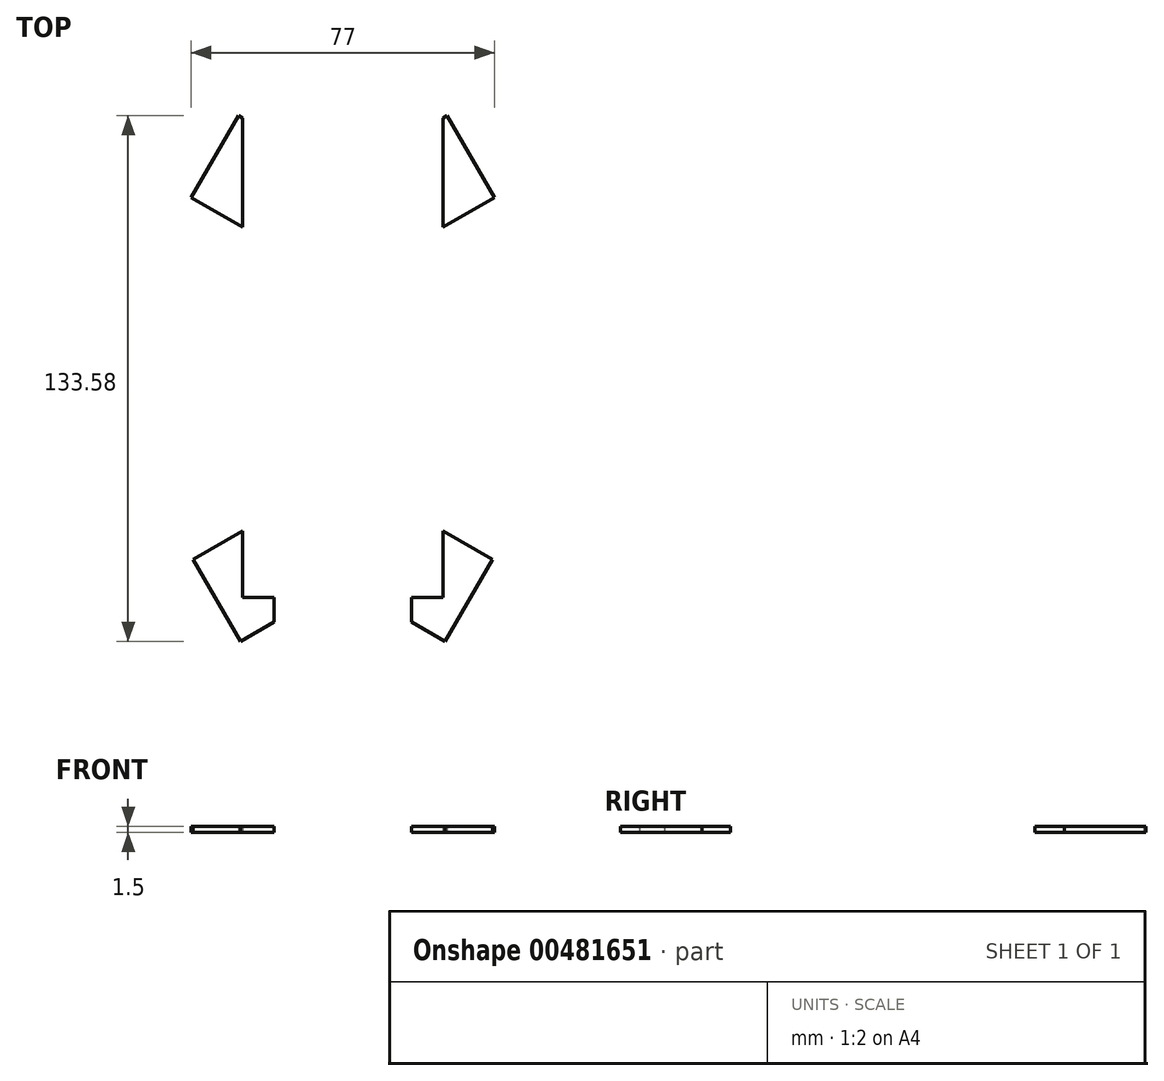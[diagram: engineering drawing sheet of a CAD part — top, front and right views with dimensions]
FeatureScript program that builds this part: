
annotation { "Feature Type Name" : "Feature", "Feature Type Description" : "" }
export const myFeature = defineFeature(function(context is Context, id is Id, definition is map)
    precondition{}
    {
        {
            var Q0;
            Q0=qCreatedBy(makeId("Top.planeOp"),FACE);
            var sketch = newSketch(context, id + "F0", { "sketchPlane" : qUnion([Q0])});
            skLineSegment(sketch, "E0", {"start": v(0, 0) * mm, "end": v(-18, 0) * mm});
            skLineSegment(sketch, "E1", {"start": v(-18, 0) * mm, "end": v(-18, -5) * mm});
            skLineSegment(sketch, "E2", {"start": v(-18, -5) * mm, "end": v(-26, -5) * mm});
            skLineSegment(sketch, "E3", {"start": v(-26, -5) * mm, "end": v(-26, -28) * mm});
            skLineSegment(sketch, "E4", {"start": v(-26, -28) * mm, "end": v(-37, -47) * mm});
            skLineSegment(sketch, "E5", {"start": v(-37, -47) * mm, "end": v(-26, -63) * mm});
            skLineSegment(sketch, "E6", {"start": v(-26, -63) * mm, "end": v(-26, -130) * mm});
            skLineSegment(sketch, "E7", {"start": v(-26, -130) * mm, "end": v(-38, -139) * mm});
            skLineSegment(sketch, "E8", {"start": v(-38, -139) * mm, "end": v(-25, -160) * mm});
            skLineSegment(sketch, "E9", {"start": v(-25, -160) * mm, "end": v(-23, -160) * mm});
            skLineSegment(sketch, "E10", {"start": v(-23, -160) * mm, "end": v(-17, -150) * mm});
            skLineSegment(sketch, "E11", {"start": v(-17, -150) * mm, "end": v(0, -150) * mm});
            skLineSegment(sketch, "E12", {"start": v(0, -150) * mm, "end": v(0, 62.6) * mm, "construction": true});
            skLineSegment(sketch, "E13.MirrorCS", {"start": v(0, 0) * mm, "end": v(18, 0) * mm});
            skLineSegment(sketch, "E14.MirrorCS", {"start": v(26, -63) * mm, "end": v(26, -130) * mm});
            skLineSegment(sketch, "E15.MirrorCS", {"start": v(18, 0) * mm, "end": v(18, -5) * mm});
            skLineSegment(sketch, "E16.MirrorCS", {"start": v(18, -5) * mm, "end": v(26, -5) * mm});
            skLineSegment(sketch, "E17.MirrorCS", {"start": v(26, -5) * mm, "end": v(26, -28) * mm});
            skLineSegment(sketch, "E18.MirrorCS", {"start": v(26, -28) * mm, "end": v(37, -47) * mm});
            skLineSegment(sketch, "E19.MirrorCS", {"start": v(37, -47) * mm, "end": v(26, -63) * mm});
            skLineSegment(sketch, "E20.MirrorCS", {"start": v(26, -130) * mm, "end": v(38, -139) * mm});
            skLineSegment(sketch, "E21.MirrorCS", {"start": v(38, -139) * mm, "end": v(25, -160) * mm});
            skLineSegment(sketch, "E22.MirrorCS", {"start": v(17, -150) * mm, "end": v(0, -150) * mm});
            skLineSegment(sketch, "E23.MirrorCS", {"start": v(23, -160) * mm, "end": v(17, -150) * mm});
            skLineSegment(sketch, "E24.MirrorCS", {"start": v(25, -160) * mm, "end": v(23, -160) * mm});
            skSolve(sketch);
        }
        {
            var Q0;
            Q0=qCreatedBy(makeId("Top.planeOp"),FACE);
            var sketch = newSketch(context, id + "F1", { "sketchPlane" : qUnion([Q0])});
            skLineSegment(sketch, "E25.bottom", {"start": v(25.5, -75) * mm, "end": v(-25.5, -75) * mm});
            skLineSegment(sketch, "E25.top", {"start": v(25.5, 75) * mm, "end": v(-25.5, 75) * mm});
            skLineSegment(sketch, "E25.left", {"start": v(25.5, -75) * mm, "end": v(25.5, 75) * mm});
            skLineSegment(sketch, "E25.right", {"start": v(-25.5, -75) * mm, "end": v(-25.5, 75) * mm});
            skPoint(sketch, "E25.middle", {"position": v(0, 0) * mm});
            skLineSegment(sketch, "E26", {"start": v(25.5, -72) * mm, "end": v(119.06, -126.02) * mm, "construction": true});
            skLineSegment(sketch, "E27", {"start": v(25.5, 33) * mm, "end": v(109.31, 81.39) * mm, "construction": true});
            skLineSegment(sketch, "E28", {"start": v(25.5, 46.86) * mm, "end": v(26.5, 47.43) * mm});
            skLineSegment(sketch, "E29", {"start": v(25.5, 19.14) * mm, "end": v(38.5, 26.65) * mm});
            skLineSegment(sketch, "E30", {"start": v(25.5, -58.14) * mm, "end": v(38, -65.36) * mm});
            skLineSegment(sketch, "E31", {"start": v(25.5, -85.86) * mm, "end": v(26, -86.15) * mm});
            skLineSegment(sketch, "E32", {"start": v(17.5, -75) * mm, "end": v(17.5, -81.24) * mm});
            skLineSegment(sketch, "E33", {"start": v(25.5, -85.86) * mm, "end": v(17.5, -81.24) * mm});
            skLineSegment(sketch, "E34", {"start": v(38.5, 26.65) * mm, "end": v(26.5, 47.43) * mm});
            skLineSegment(sketch, "E35", {"start": v(38, -65.36) * mm, "end": v(26, -86.15) * mm});
            skLineSegment(sketch, "E36.MirrorCS", {"start": v(-25.5, -85.86) * mm, "end": v(-17.5, -81.24) * mm});
            skLineSegment(sketch, "E37.MirrorCS", {"start": v(-25.5, -85.86) * mm, "end": v(-26, -86.15) * mm});
            skLineSegment(sketch, "E38.MirrorCS", {"start": v(-25.5, 46.86) * mm, "end": v(-26.5, 47.43) * mm});
            skLineSegment(sketch, "E39.MirrorCS", {"start": v(-17.5, -75) * mm, "end": v(-17.5, -81.24) * mm});
            skLineSegment(sketch, "E40.MirrorCS", {"start": v(-38.5, 26.65) * mm, "end": v(-26.5, 47.43) * mm});
            skLineSegment(sketch, "E41.MirrorCS", {"start": v(-38, -65.36) * mm, "end": v(-26, -86.15) * mm});
            skLineSegment(sketch, "E42.MirrorCS", {"start": v(-25.5, 19.14) * mm, "end": v(-38.5, 26.65) * mm});
            skLineSegment(sketch, "E43.MirrorCS", {"start": v(-25.5, -58.14) * mm, "end": v(-38, -65.36) * mm});
            skSolve(sketch);
        }
        {
            var Q0;
            {var subQ6=sQuery(id+"F1.wireOp",EDGE,"E25.top");Q0=makeQuery(id+"F1.imprint","IMPRINT",FACE,{"disambiguationData":[TD([[makeQuery(id+"F1.imprint","IMPRINT",EDGE,{"derivedFrom":subQ6}),1.0]])]});}
            var Q1;
            {var subQ0=sQuery(id+"F1.wireOp",EDGE,"E38.MirrorCS");Q1=makeQuery(id+"F1.imprint","IMPRINT",FACE,{"disambiguationData":[TD([[makeQuery(id+"F1.imprint","IMPRINT",EDGE,{"derivedFrom":subQ0}),1.0]])]});}
            var Q2;
            {var subQ0=sQuery(id+"F1.wireOp",EDGE,"E28");Q2=makeQuery(id+"F1.imprint","IMPRINT",FACE,{"disambiguationData":[TD([[makeQuery(id+"F1.imprint","IMPRINT",EDGE,{"derivedFrom":subQ0}),-1.0]])]});}
            var Q3;
            {var subQ0=sQuery(id+"F1.wireOp",EDGE,"E30");Q3=makeQuery(id+"F1.imprint","IMPRINT",FACE,{"disambiguationData":[TD([[makeQuery(id+"F1.imprint","IMPRINT",EDGE,{"derivedFrom":subQ0}),-1.0]])]});}
            var Q4;
            Q4=makeQuery(id+"F1.imprint","IMPRINT",FACE,{"disambiguationData":[TD([[makeQuery(id+"F1.imprint","IMPRINT",EDGE,{"derivedFrom":sQuery(id+"F1.wireOp",EDGE,"E36.MirrorCS")}),1.0]])]});
            extrude(context, id + "F2", {"entities" : qUnion([Q0, Q1, Q2, Q3, Q4]), "depth" : 1.5 * mm, "offsetDistance" : 25 * mm});
        }
    });
